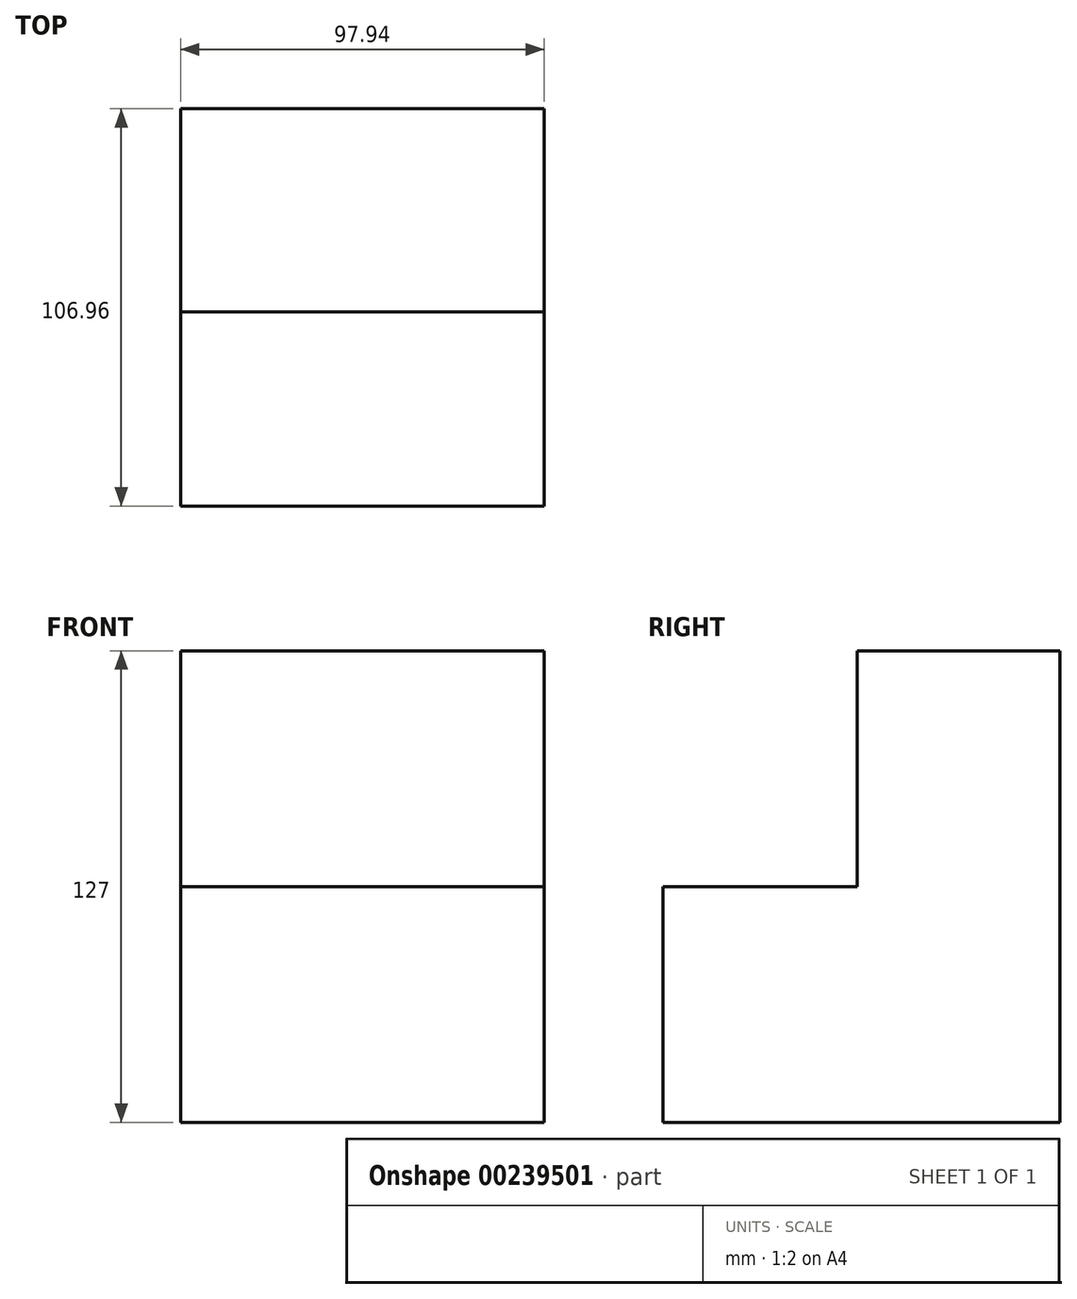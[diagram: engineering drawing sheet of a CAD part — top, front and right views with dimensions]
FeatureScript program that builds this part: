
annotation { "Feature Type Name" : "Feature", "Feature Type Description" : "" }
export const myFeature = defineFeature(function(context is Context, id is Id, definition is map)
    precondition{}
    {
        {
            var Q0;
            Q0=qCreatedBy(makeId("Top.planeOp"),FACE);
            var sketch = newSketch(context, id + "F0", { "sketchPlane" : qUnion([Q0])});
            skLineSegment(sketch, "E0.bottom", {"start": v(48.97, 27.32) * mm, "end": v(-48.97, 27.32) * mm});
            skLineSegment(sketch, "E0.top", {"start": v(48.97, -27.32) * mm, "end": v(-48.97, -27.32) * mm});
            skLineSegment(sketch, "E0.left", {"start": v(48.97, 27.32) * mm, "end": v(48.97, -27.32) * mm});
            skLineSegment(sketch, "E0.right", {"start": v(-48.97, 27.32) * mm, "end": v(-48.97, -27.32) * mm});
            skPoint(sketch, "E0.middle", {"position": v(0, 0) * mm});
            skSolve(sketch);
        }
        {
            var Q0;
            Q0 = qSketchRegion(id + "F0", true);
            extrude(context, id + "F1", {"entities" : qUnion([Q0]), "endBound" : BoundingType.SYMMETRIC, "depth" : 127 * mm});
        }
        {
            var Q0;
            Q0=makeQuery(id+"F1.opExtrude","SWEPT_FACE",FACE,{"disambiguationData":[OSD([sQuery(id+"F0.wireOp",EDGE,"E0.top")])]});
            var sketch = newSketch(context, id + "F2", { "sketchPlane" : qUnion([Q0])});
            skLineSegment(sketch, "E1.bottom", {"start": v(-48.97, -63.5) * mm, "end": v(48.97, -63.5) * mm});
            skLineSegment(sketch, "E1.top", {"start": v(-48.97, 0) * mm, "end": v(48.97, 0) * mm});
            skLineSegment(sketch, "E1.left", {"start": v(-48.97, -63.5) * mm, "end": v(-48.97, 0) * mm});
            skLineSegment(sketch, "E1.right", {"start": v(48.97, -63.5) * mm, "end": v(48.97, 0) * mm});
            skSolve(sketch);
        }
        {
            var Q0;
            Q0 = qSketchRegion(id + "F2", true);
            extrude(context, id + "F3", {"entities" : qUnion([Q0]), "operationType" : NewBodyOperationType.ADD, "depth" : 52.32 * mm});
        }
    });
